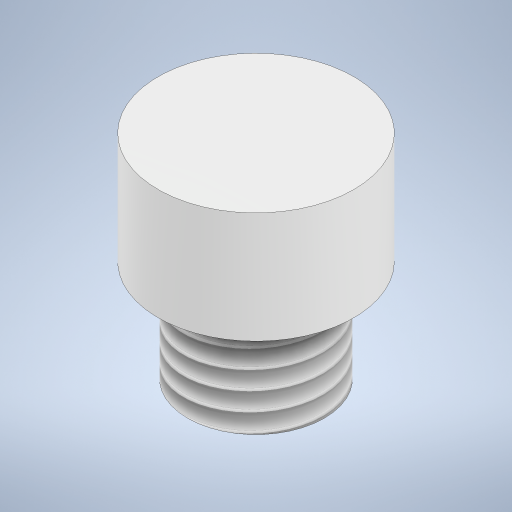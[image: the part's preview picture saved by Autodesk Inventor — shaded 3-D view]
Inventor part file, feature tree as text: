
AUTODESK INVENTOR PART (.ipt)
format: ipt  version: 2024 (Build 280153000, 153)  size: 289,280 bytes
history: native  units: mm
features: extrude x11, sketch x8, other x1, plane x1, thread x1
ambient origin geometry x8: Origin, YZ Plane, XZ Plane, XY Plane, X Axis, Y Axis, Z Axis, Center Point
bodies: Body1 (feature_tree)
feature tree (22):
  other  "Sólido1"
  extrude  "Extrusión1"  Depth=26.65mm
  plane  "Plano de trabajo2"
  extrude  "Extrusión4"  [1 undecoded]
  extrude  "Extrusión5"  Depth=18.97mm TaperAngle=0.0deg
  extrude  "Extrusión6"  Depth=13.4mm
  extrude  "Extrusión7"  Depth=18.97mm TaperAngle=0.0deg
  thread  "Rosca2"  [1 undecoded]
  extrude  "Extrusión8"  Depth=14.87mm TaperAngle=0.0deg
  extrude  "Extrusión9"  Depth=8.47mm TaperAngle=0.0deg
  extrude  "Extrusión10"  Depth=8.47mm TaperAngle=0.0deg
  extrude  "Extrusión11"  Depth=8.47mm TaperAngle=0.0deg
  extrude  "Extrusión12"  Depth=10.0mm TaperAngle=0.0deg
  extrude  "Extrusión13"  Depth=10.0mm
  sketch  "Boceto15"  dims[d38=53.22mm d39=0.0mm d40=8.47mm d41=0.0mm d42=8.47mm d43=0.0mm d44=10.0mm d45=0.0mm d46=18.6mm]
  sketch  "Boceto5"  dims[d0=18.0mm d1=26.65mm]
  sketch  "Boceto9"  dims[d2=23.6mm d3=0.0mm d17=-18.5mm]
  sketch  "Boceto10"  dims[d18=13.6mm d19=18.97mm d20=0.0mm]
  sketch  "Boceto11"  dims[d21=18.97mm d22=0.0mm d25=13.4mm]
  sketch  "Boceto12"  dims[d26=18.6mm d27=18.97mm d28=0.0mm d29=17.0mm]
  sketch  "Boceto13"  dims[d30=18.97mm d31=0.0mm d32=14.87mm d33=0.0mm]
  sketch  "Boceto14"  dims[d34=8.47mm d35=0.0mm d36=1.0mm d37=0.0mm]
note: 2 required parameter values undecoded (feature->parameter linkage not recoverable at this tier; creation-order binding heuristic only, values carry confidence <= 0.55)
